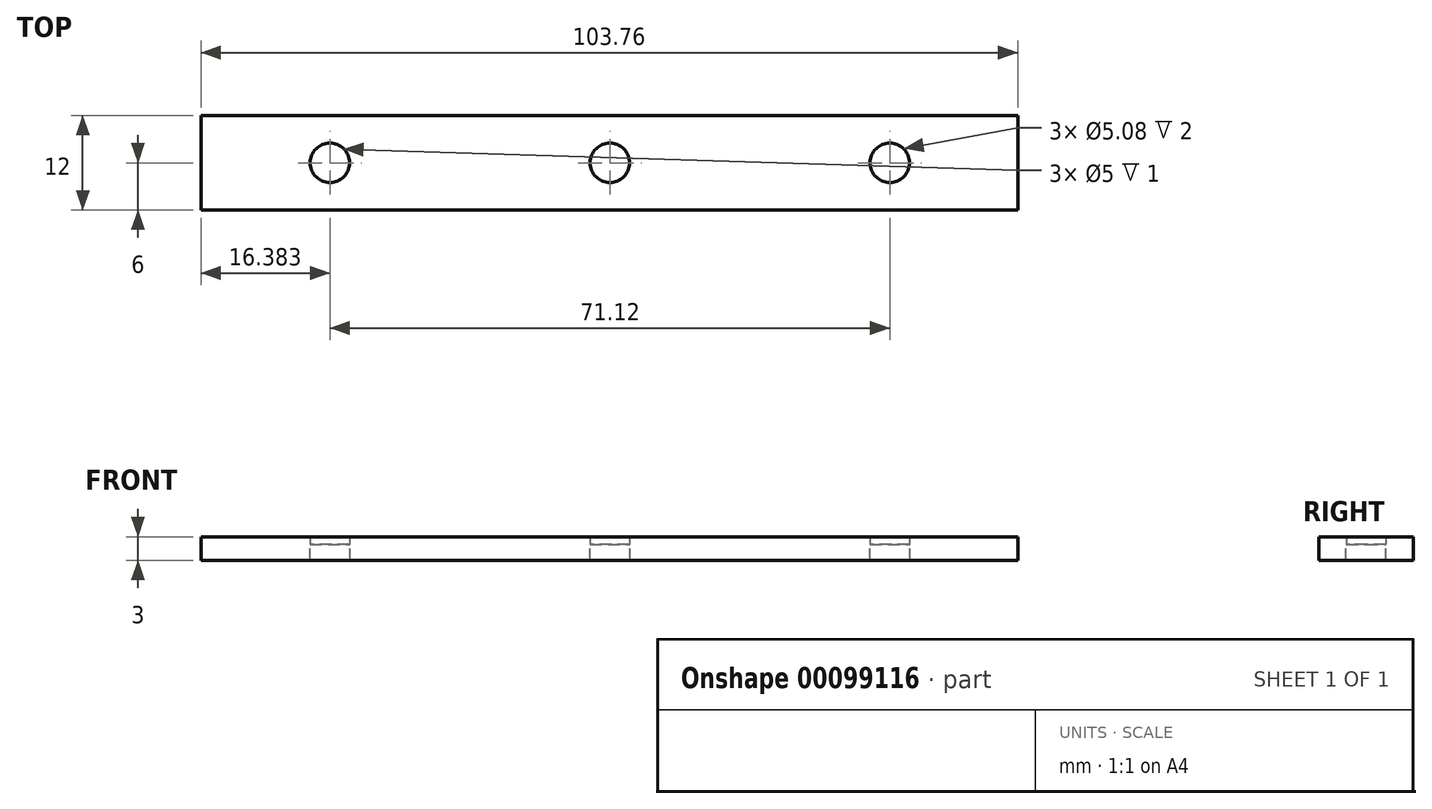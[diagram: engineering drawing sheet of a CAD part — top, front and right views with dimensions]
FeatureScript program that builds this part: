
annotation { "Feature Type Name" : "Feature", "Feature Type Description" : "" }
export const myFeature = defineFeature(function(context is Context, id is Id, definition is map)
    precondition{}
    {
        {
            var Q0;
            Q0=qCreatedBy(makeId("Right.planeOp"),FACE);
            var sketch = newSketch(context, id + "F0", { "sketchPlane" : qUnion([Q0])});
            skLineSegment(sketch, "E0", {"start": v(0, 0) * mm, "end": v(0, 2) * mm});
            skLineSegment(sketch, "E1", {"start": v(0, 0) * mm, "end": v(20, 0) * mm});
            skLineSegment(sketch, "E2", {"start": v(20, 0) * mm, "end": v(20, 2) * mm});
            skLineSegment(sketch, "E3", {"start": v(20, 2) * mm, "end": v(0, 2) * mm});
            skSolve(sketch);
        }
        {
            var Q0;
            Q0=makeQuery(id+"F0.imprint","IMPRINT",FACE,{"disambiguationData":[TD([[makeQuery(id+"F0.imprint","IMPRINT",EDGE,{"derivedFrom":sQuery(id+"F0.wireOp",EDGE,"E0")}),-1.0]])]});
            extrude(context, id + "F1", {"entities" : qUnion([Q0]), "depth" : 103.76 * mm});
        }
        {
            var Q0;
            Q0=makeQuery(id+"F1.opExtrude","SWEPT_FACE",FACE,{"disambiguationData":[OSD([sQuery(id+"F0.wireOp",EDGE,"E1")])]});
            var sketch = newSketch(context, id + "F2", { "sketchPlane" : qUnion([Q0])});
            skCircle(sketch, "E4", {"center": v(87.5, -10) * mm, "radius": 2.54 * mm});
            skCircle(sketch, "E5", {"center": v(16.38, -10) * mm, "radius": 2.54 * mm});
            skLineSegment(sketch, "E6", {"start": v(16.38, -10) * mm, "end": v(0, -10) * mm, "construction": true});
            skPoint(sketch, "E6.endSnap0", {"position": v(0, -10) * mm});
            skCircle(sketch, "E7", {"center": v(51.94, -10) * mm, "radius": 2.54 * mm});
            skSolve(sketch);
        }
        {
            var Q0;
            Q0=qSketchRegion(id+"F2",true);
            extrude(context, id + "F3", {"entities" : qUnion([Q0]), "operationType" : NewBodyOperationType.REMOVE, "endBound" : BoundingType.SYMMETRIC, "depth" : 25.4 * mm, "offsetDistance" : 25.4 * mm});
        }
        {
            var Q0;
            Q0=makeQuery(id+"F1.opExtrude","SWEPT_FACE",FACE,{"disambiguationData":[OSD([sQuery(id+"F0.wireOp",EDGE,"E3")])]});
            var sketch = newSketch(context, id + "F4", { "sketchPlane" : qUnion([Q0])});
            skLineSegment(sketch, "E8.bottom", {"start": v(0, 16) * mm, "end": v(103.76, 16) * mm});
            skLineSegment(sketch, "E8.top", {"start": v(0, 4) * mm, "end": v(103.76, 4) * mm});
            skLineSegment(sketch, "E8.left", {"start": v(0, 16) * mm, "end": v(0, 4) * mm});
            skLineSegment(sketch, "E8.right", {"start": v(103.76, 16) * mm, "end": v(103.76, 4) * mm});
            skCircle(sketch, "E9", {"center": v(16.38, 10) * mm, "radius": 2.5 * mm});
            skCircle(sketch, "E10", {"center": v(51.94, 10) * mm, "radius": 2.5 * mm});
            skCircle(sketch, "E11", {"center": v(87.5, 10) * mm, "radius": 2.5 * mm});
            skSolve(sketch);
        }
        {
            var Q0;
            Q0 = qSketchRegion(id + "F4", true);
            extrude(context, id + "F5", {"entities" : qUnion([Q0]), "operationType" : NewBodyOperationType.ADD, "depth" : 1 * mm, "offsetDistance" : 25 * mm});
        }
        {
            var Q0;
            Q0=makeQuery(id+"F5.boolean.opBoolean","MERGE",FACE,{"derivedFrom":[makeQuery(id+"F1.opExtrude","CAP_FACE",FACE,{"disambiguationData":[OSD([sQuery(id+"F0.wireOp",EDGE,"E0"),sQuery(id+"F0.wireOp",EDGE,"E1"),sQuery(id+"F0.wireOp",EDGE,"E2"),sQuery(id+"F0.wireOp",EDGE,"E3")])],"isStart":true}),makeQuery(id+"F5.opExtrude","SWEPT_FACE",FACE,{"disambiguationData":[OSD([sQuery(id+"F4.wireOp",EDGE,"E8.left")])]})]});
            var sketch = newSketch(context, id + "F6", { "sketchPlane" : qUnion([Q0])});
            skLineSegment(sketch, "E12.bottom", {"start": v(-16, 2) * mm, "end": v(-20.98, 2) * mm});
            skLineSegment(sketch, "E12.top", {"start": v(-16, -0.72) * mm, "end": v(-20.98, -0.72) * mm});
            skLineSegment(sketch, "E12.left", {"start": v(-16, 2) * mm, "end": v(-16, -0.72) * mm});
            skLineSegment(sketch, "E12.right", {"start": v(-20.98, 2) * mm, "end": v(-20.98, -0.72) * mm});
            skLineSegment(sketch, "E13.bottom", {"start": v(-4, 2) * mm, "end": v(1.41, 2) * mm});
            skLineSegment(sketch, "E13.top", {"start": v(-4, -0.59) * mm, "end": v(1.41, -0.59) * mm});
            skLineSegment(sketch, "E13.left", {"start": v(-4, 2) * mm, "end": v(-4, -0.59) * mm});
            skLineSegment(sketch, "E13.right", {"start": v(1.41, 2) * mm, "end": v(1.41, -0.59) * mm});
            skSolve(sketch);
        }
        {
            var Q0;
            Q0 = qSketchRegion(id + "F6", true);
            extrude(context, id + "F7", {"entities" : qUnion([Q0]), "operationType" : NewBodyOperationType.REMOVE, "endBound" : BoundingType.THROUGH_ALL, "oppositeDirection" : true, "depth" : 25 * mm, "offsetDistance" : 25 * mm});
        }
    });
